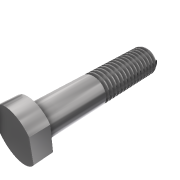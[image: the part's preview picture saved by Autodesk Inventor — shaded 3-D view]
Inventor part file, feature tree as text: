
AUTODESK INVENTOR PART (.ipt)
format: ipt  version: 2016 (Build 200138000, 138)  size: 497,152 bytes
history: native  units: mm
features: sketch x8, extrude x6, plane x3, hole x1, chamfer x1, helix x1, projected_geometry x1
ambient origin geometry x8: Origin, YZ Plane, XZ Plane, XY Plane, X Axis, Y Axis, Z Axis, Center Point
bodies: Solid1 (feature_tree)
feature tree (21):
  plane  "Work Plane1"
  extrude  "Extrusion1"  Depth=36.5mm TaperAngle=0.0deg
  extrude  "Extrusion2"  Depth=4.5mm TaperAngle=0.0deg
  plane  "Work Plane2"
  extrude  "Extrusion4"  Depth=1.0mm
  hole  "Hole1"  [1 undecoded]
  extrude  "Extrusion5"  Depth=6.8mm
  extrude  "Extrusion6"  Depth=0.3mm TaperAngle=45.0deg
  chamfer  "Chamfer2"  Distance=0.67mm
  plane  "Work Plane3"
  helix  "Coil1"  [1 undecoded]
  extrude  "Extrusion7"  Depth=0.1mm
  sketch  "Sketch1"  dims[d0=8.0mm d1=36.5mm d2=0.0mm]
  sketch  "Sketch2"  dims[d3=13.0mm d4=4.5mm d5=0.0mm]
  sketch  "Sketch4"  dims[d16=1.0mm d17=1.0mm]
  sketch  "Sketch5"  dims[d18=0.9mm d19=0.0mm]
  sketch  "Sketch6"  dims[d20=2.459mm d21=10.0mm d22=5.0mm d23=2.0mm d24=90.0deg d25=13.0mm d26=20.594885mm d27=0.2mm d28=0.0mm]
  sketch  "Sketch7"  dims[d29=5.5mm d30=6.8mm]
  sketch  "Sketch8"  dims[d31=1.0mm d32=0.0mm d33=0.3mm d34=2.0mm d35=45.0deg]
  sketch  "Sketch9"  dims[d36=12.217305mm d38=0.67mm d39=0.7mm d40=1.25mm d41=10.0mm d42=160.0mm d43=0.0mm d44=90.0deg d45=90.0deg d46=90.0deg d47=90.0deg d48=0.1mm d49=10.0mm d50=0.0mm d51=9.599311mm]
  projected_geometry  "Projected Loop1"
note: 2 required parameter values undecoded (feature->parameter linkage not recoverable at this tier; creation-order binding heuristic only, values carry confidence <= 0.55)
